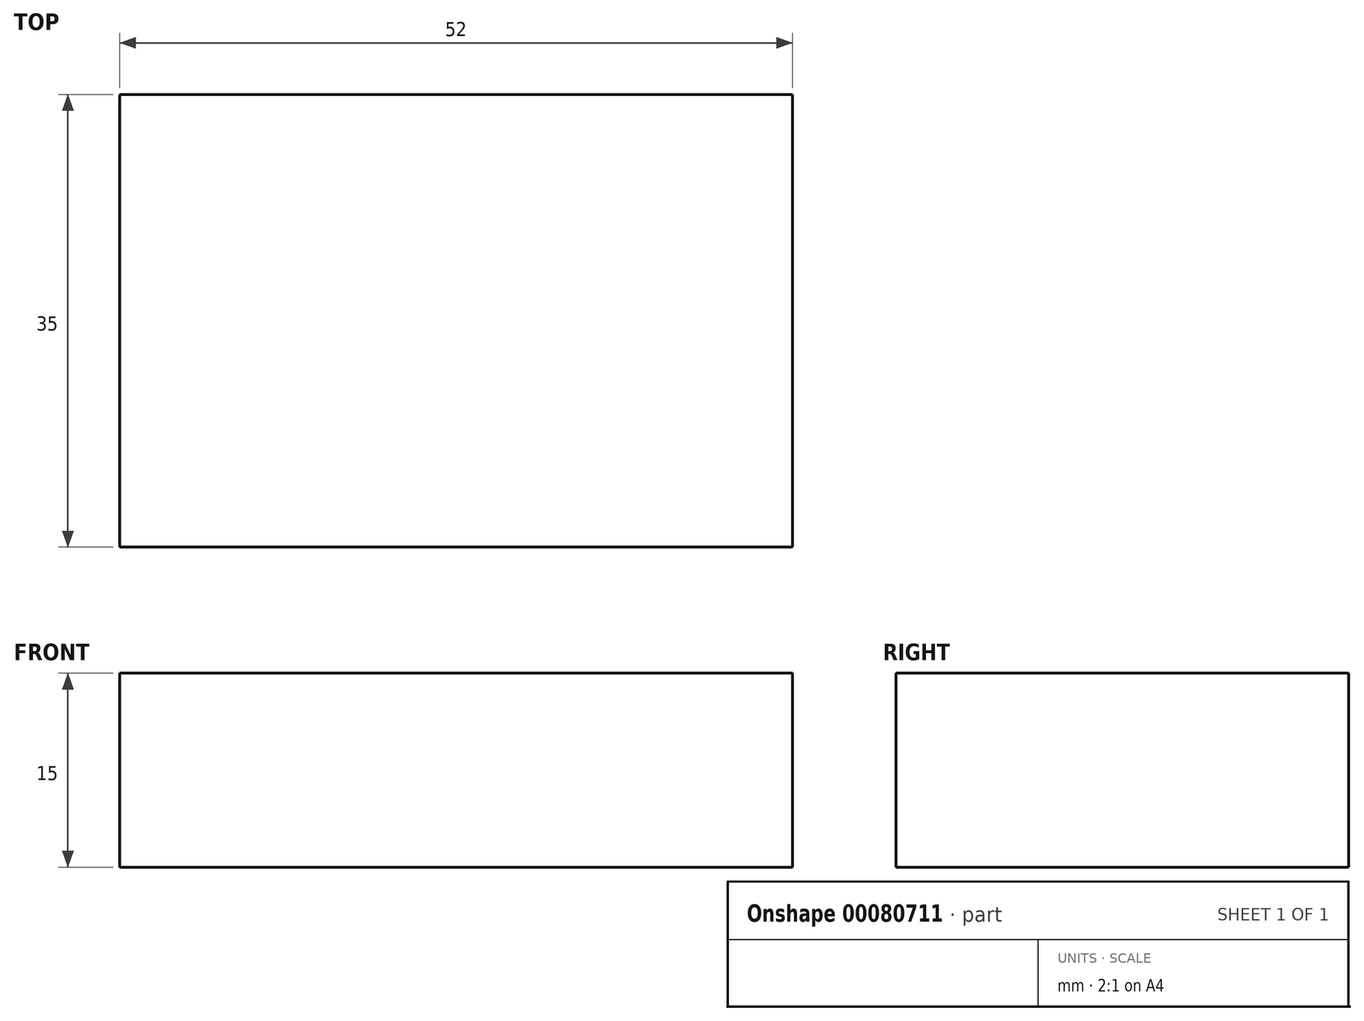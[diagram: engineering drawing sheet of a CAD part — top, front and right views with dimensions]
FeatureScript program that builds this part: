
annotation { "Feature Type Name" : "Feature", "Feature Type Description" : "" }
export const myFeature = defineFeature(function(context is Context, id is Id, definition is map)
    precondition{}
    {
        {
            var Q0;
            Q0=qCreatedBy(makeId("Top.planeOp"),FACE);
            var sketch = newSketch(context, id + "F0", { "sketchPlane" : qUnion([Q0])});
            skLineSegment(sketch, "E0.bottom", {"start": v(26, -17.5) * mm, "end": v(-26, -17.5) * mm});
            skLineSegment(sketch, "E0.top", {"start": v(26, 17.5) * mm, "end": v(-26, 17.5) * mm});
            skLineSegment(sketch, "E0.left", {"start": v(26, -17.5) * mm, "end": v(26, 17.5) * mm});
            skLineSegment(sketch, "E0.right", {"start": v(-26, -17.5) * mm, "end": v(-26, 17.5) * mm});
            skPoint(sketch, "E0.middle", {"position": v(0, 0) * mm});
            skSolve(sketch);
        }
        {
            var Q0;
            Q0 = qSketchRegion(id + "F0", true);
            extrude(context, id + "F1", {"entities" : qUnion([Q0]), "depth" : 15 * mm});
        }
    });
